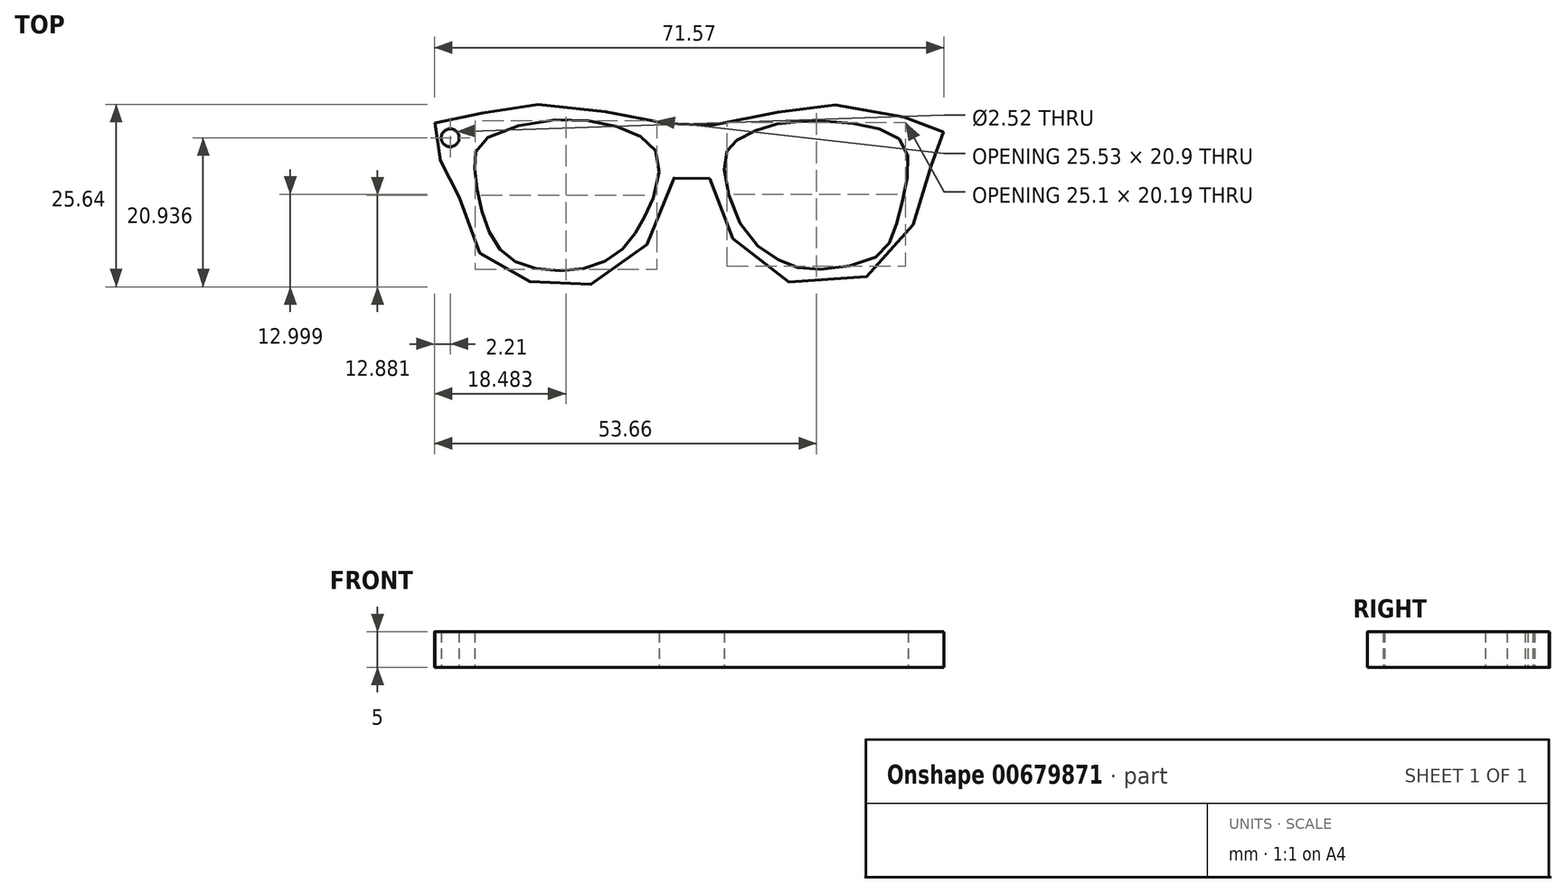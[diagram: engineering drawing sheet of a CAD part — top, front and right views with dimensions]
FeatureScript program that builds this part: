
annotation { "Feature Type Name" : "Feature", "Feature Type Description" : "" }
export const myFeature = defineFeature(function(context is Context, id is Id, definition is map)
    precondition{}
    {
        {
            var Q0;
            Q0=qCreatedBy(makeId("Top.planeOp"),FACE);
            var sketch = newSketch(context, id + "F0", { "sketchPlane" : qUnion([Q0])});
            skFitSpline(sketch, "E0", {"points": [v(-32.47, 22.51) * mm, v(-35.21, 22.39) * mm, v(-38.33, 22.7) * mm, v(-42.26, 23.38) * mm, v(-49.25, 24.7) * mm, v(-55.86, 25.33) * mm, v(-59.8, 25.33) * mm, v(-64.66, 24.2) * mm, v(-68.28, 23.32) * mm, v(-71.35, 22.82) * mm, v(-71.35, 21.82) * mm, v(-71.35, 19.27) * mm, v(-70.27, 17.15) * mm, v(-69.02, 16.15) * mm, v(-68.15, 12.97) * mm, v(-66.22, 7.66) * mm, v(-64.66, 3.92) * mm, v(-60.54, 1.36) * mm, v(-55.49, 0) * mm, v(-50.06, 0) * mm, v(-44.63, 2.42) * mm, v(-39.58, 9.53) * mm, v(-37.7, 15.27) * mm, v(-36.02, 16.33) * mm, v(-33.34, 15.77) * mm, v(-31.66, 10.97) * mm, v(-28.79, 5.54) * mm, v(-23.17, 1.05) * mm, v(-14.75, 0) * mm, v(-7.01, 3.73) * mm, v(-3.96, 9.41) * mm, v(-2.52, 15.09) * mm, v(-0.78, 17.77) * mm, v(0, 18.2) * mm, v(0, 21.2) * mm, v(0, 22.7) * mm, v(-2.65, 23.13) * mm, v(-10.45, 24.82) * mm, v(-15.94, 25.33) * mm, v(-20.24, 24.88) * mm, v(-26.35, 23.63) * mm, v(-32.47, 22.51) * mm]});
            skFitSpline(sketch, "E1", {"points": [v(-64.77, 10.38) * mm, v(-65.63, 14.8) * mm, v(-65.8, 17.88) * mm, v(-64.88, 20.14) * mm, v(-55.87, 23.11) * mm, v(-46.64, 22.52) * mm, v(-41.63, 20.3) * mm, v(-39.9, 17.29) * mm, v(-41.03, 11.46) * mm, v(-42.54, 8.55) * mm, v(-44.38, 5.74) * mm, v(-47.72, 3.26) * mm, v(-52.1, 2.13) * mm, v(-57.38, 2.4) * mm, v(-61, 3.85) * mm, v(-63.26, 6.55) * mm, v(-64.77, 10.38) * mm]});
            skFitSpline(sketch, "E2", {"points": [v(-30.35, 18.85) * mm, v(-28.79, 20.52) * mm, v(-24.36, 22.4) * mm, v(-19.13, 23.06) * mm, v(-11.63, 22.63) * mm, v(-6.18, 20.58) * mm, v(-4.89, 17.29) * mm, v(-5.8, 11.57) * mm, v(-7.2, 6.71) * mm, v(-9.64, 3.85) * mm, v(-17.62, 2.23) * mm, v(-22.15, 3.1) * mm, v(-27.22, 6.82) * mm, v(-30.62, 14.8) * mm, v(-30.35, 18.85) * mm]});
            skCircle(sketch, "E3", {"center": v(-69.25, 20.73) * mm, "radius": 1.26 * mm});
            skSolve(sketch);
        }
        {
            var Q0;
            Q0 = qSketchRegion(id + "F0", true);
            extrude(context, id + "F1", {"entities" : qUnion([Q0]), "depth" : 5 * mm, "offsetDistance" : 25 * mm});
        }
        {
            var Q0;
            Q0 = qSketchRegion(id + "F0", true);
            extrude(context, id + "F2", {"entities" : qUnion([Q0]), "operationType" : NewBodyOperationType.REMOVE, "oppositeDirection" : true, "depth" : 5 * mm, "offsetDistance" : 25 * mm});
        }
    });
